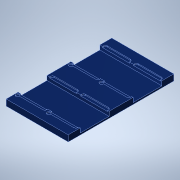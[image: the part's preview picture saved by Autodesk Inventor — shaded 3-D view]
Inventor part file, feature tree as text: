
AUTODESK INVENTOR PART (.ipt)
format: ipt  version: 2022 (Build 260153000, 153)  size: 209,920 bytes
history: native  units: in
note: dims shown in document units (in); Inventor stores cm internally (conversion verified against a paired STEP export)
features: extrude x3, sketch x3
ambient origin geometry x8: Origin, YZ Plane, XZ Plane, XY Plane, X Axis, Y Axis, Z Axis, Center Point
bodies: Solid1 (feature_tree)
feature tree (6):
  extrude  "Extrusion1"  Depth=8.5in
  extrude  "Extrusion12"  Depth=2.7953in
  extrude  "Extrusion14"  Depth=0.3937in
  sketch  "Sketch1"  dims[d0=5.0in d1=8.5in]
  sketch  "Sketch13"  dims[d2=0.5in d3=0.0in d142=2.7953in]
  sketch  "Sketch15"  dims[d143=2.1654in d146=1.2992in d147=1.2008in d148=2.125in d149=2.125in d150=0.1575in d151=0.315in d152=0.7874in d154=2.5in d155=0.7874in d157=4.25in d160=0.0787in d161=0.0in d171=2.3228in d172=0.9636in d173=0.9636in d174=0.3543in d175=0.0in d176=0.7874in d178=4.25in d179=0.3937in d181=0.3937in]
